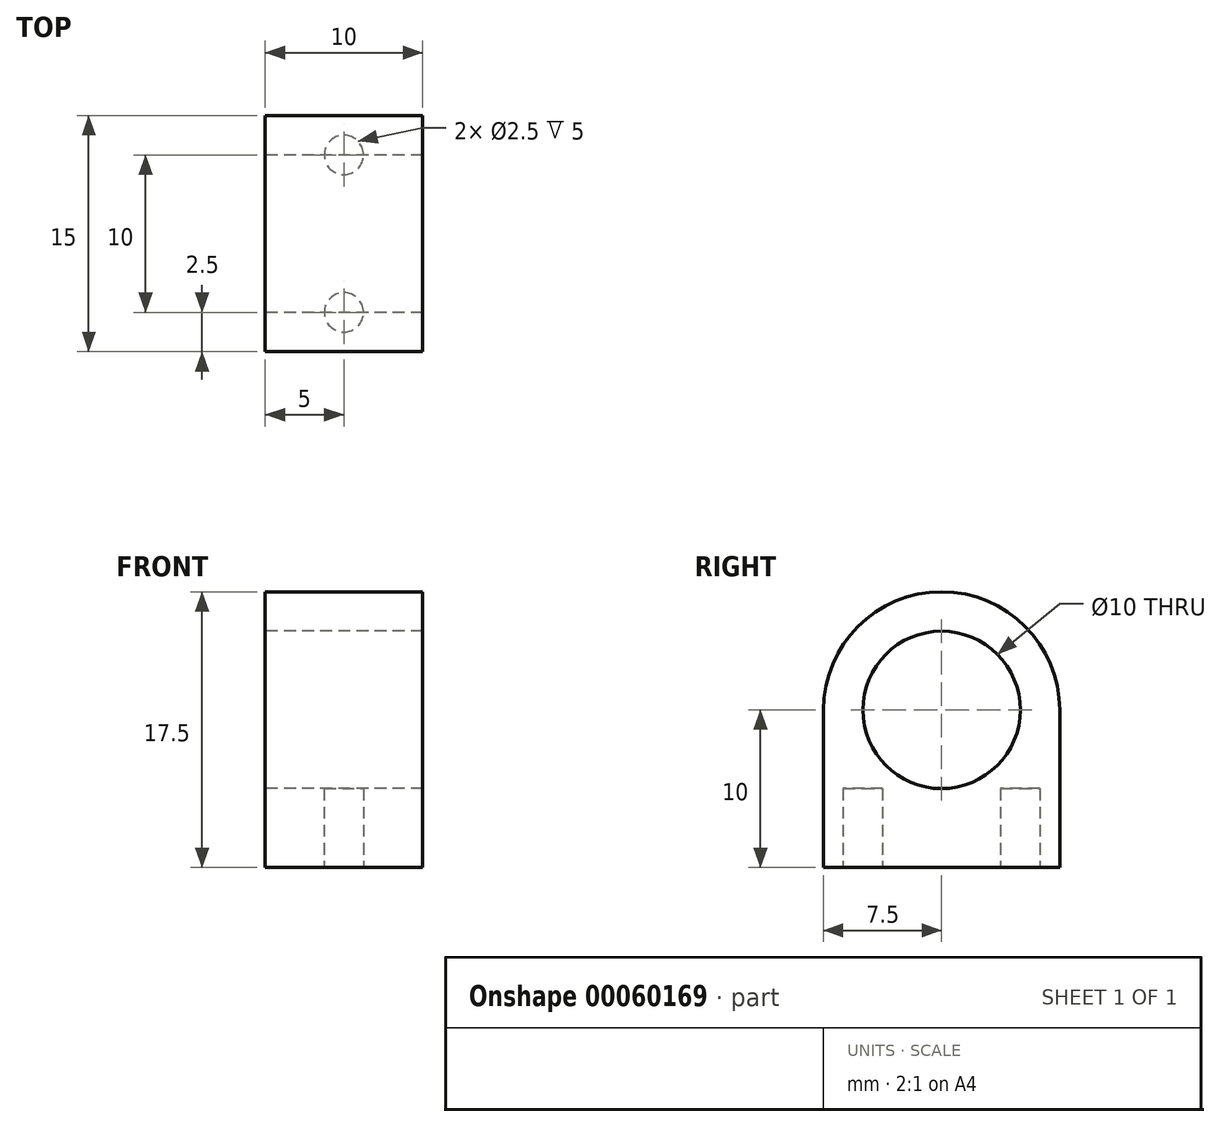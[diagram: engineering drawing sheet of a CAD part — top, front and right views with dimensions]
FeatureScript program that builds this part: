
annotation { "Feature Type Name" : "Feature", "Feature Type Description" : "" }
export const myFeature = defineFeature(function(context is Context, id is Id, definition is map)
    precondition{}
    {
        {
            var Q0;
            Q0=qCreatedBy(makeId("Right.planeOp"),FACE);
            var sketch = newSketch(context, id + "F0", { "sketchPlane" : qUnion([Q0])});
            skCircle(sketch, "E0", {"center": v(0, 0) * mm, "radius": 5 * mm});
            skArc(sketch, "E1", {"start": v(7.5, 0) * mm, "mid": v(0, 7.5) * mm, "end": v(-7.5, 0) * mm});
            skLineSegment(sketch, "E2", {"start": v(-7.5, 0) * mm, "end": v(-7.5, -10) * mm});
            skLineSegment(sketch, "E3", {"start": v(-7.5, -10) * mm, "end": v(7.5, -10) * mm});
            skLineSegment(sketch, "E4", {"start": v(7.5, -10) * mm, "end": v(7.5, 0) * mm});
            skSolve(sketch);
        }
        {
            var Q0;
            Q0=makeQuery(id+"F0.imprint","IMPRINT",FACE,{"disambiguationData":[TD([[makeQuery(id+"F0.imprint","IMPRINT",EDGE,{"derivedFrom":sQuery(id+"F0.wireOp",EDGE,"E0")}),-1.0]])]});
            extrude(context, id + "F1", {"entities" : qUnion([Q0]), "depth" : 10 * mm, "symmetric" : true});
        }
        {
            var Q0;
            Q0=makeQuery(id+"F1.opExtrude","SWEPT_FACE",FACE,{"disambiguationData":[OSD([sQuery(id+"F0.wireOp",EDGE,"E3")])]});
            var sketch = newSketch(context, id + "F2", { "sketchPlane" : qUnion([Q0])});
            skCircle(sketch, "E5", {"center": v(0, -5) * mm, "radius": 1.25 * mm});
            skCircle(sketch, "E6", {"center": v(0, 5) * mm, "radius": 1.25 * mm});
            skSolve(sketch);
        }
        {
            var Q0;
            Q0=qSketchRegion(id+"F2",true);
            extrude(context, id + "F3", {"entities" : qUnion([Q0]), "operationType" : NewBodyOperationType.REMOVE, "oppositeDirection" : true, "depth" : 5 * mm});
        }
    });
